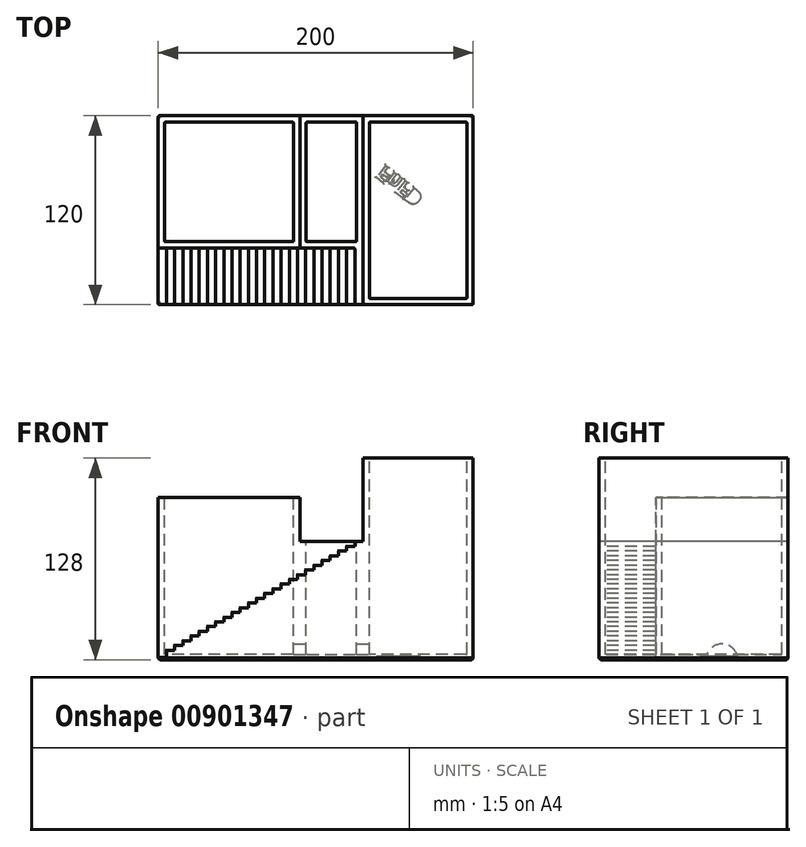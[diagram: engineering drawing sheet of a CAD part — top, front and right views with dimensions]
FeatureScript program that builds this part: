
annotation { "Feature Type Name" : "Feature", "Feature Type Description" : "" }
export const myFeature = defineFeature(function(context is Context, id is Id, definition is map)
    precondition{}
    {
        {
            var Q0;
            Q0=qCreatedBy(makeId("Top.planeOp"),FACE);
            var sketch = newSketch(context, id + "F0", { "sketchPlane" : qUnion([Q0])});
            skLineSegment(sketch, "E0.bottom", {"start": v(-100, -60) * mm, "end": v(100, -60) * mm});
            skLineSegment(sketch, "E0.top", {"start": v(-100, 60) * mm, "end": v(100, 60) * mm});
            skLineSegment(sketch, "E0.left", {"start": v(-100, -60) * mm, "end": v(-100, 60) * mm});
            skLineSegment(sketch, "E0.right", {"start": v(100, -60) * mm, "end": v(100, 60) * mm});
            skPoint(sketch, "E0.middle", {"position": v(0, 0) * mm});
            skSolve(sketch);
        }
        {
            var Q0;
            Q0=makeQuery(id+"F0.imprint","IMPRINT",FACE,{"disambiguationData":[TD([[makeQuery(id+"F0.imprint","IMPRINT",EDGE,{"derivedFrom":sQuery(id+"F0.wireOp",EDGE,"E0.bottom")}),1.0]])]});
            extrude(context, id + "F1", {"entities" : qUnion([Q0]), "depth" : 128 * mm, "offsetDistance" : 25 * mm});
        }
        {
            var Q0;
            Q0=makeQuery(id+"F1.opExtrude","SWEPT_FACE",FACE,{"disambiguationData":[OSD([sQuery(id+"F0.wireOp",EDGE,"E0.bottom")])]});
            var sketch = newSketch(context, id + "F2", { "sketchPlane" : qUnion([Q0])});
            skLineSegment(sketch, "E1.bottom", {"start": v(-100, 128) * mm, "end": v(30, 128) * mm});
            skLineSegment(sketch, "E1.top", {"start": v(-100, 75) * mm, "end": v(30, 75) * mm});
            skLineSegment(sketch, "E1.left", {"start": v(-100, 128) * mm, "end": v(-100, 75) * mm});
            skLineSegment(sketch, "E1.right", {"start": v(30, 128) * mm, "end": v(30, 75) * mm});
            skLineSegment(sketch, "E2", {"start": v(-100, 0) * mm, "end": v(30, 75) * mm, "construction": true});
            skLineSegment(sketch, "E3", {"start": v(-100, 0) * mm, "end": v(-100, 3) * mm});
            skLineSegment(sketch, "E4", {"start": v(-100, 3) * mm, "end": v(-94.8, 3) * mm});
            skLineSegment(sketch, "E5", {"start": v(-94.8, 3) * mm, "end": v(-94.8, 6) * mm});
            skLineSegment(sketch, "E6", {"start": v(-94.8, 6) * mm, "end": v(-89.6, 6) * mm});
            skLineSegment(sketch, "E7", {"start": v(-89.6, 6) * mm, "end": v(-89.6, 9) * mm});
            skLineSegment(sketch, "E8", {"start": v(-89.6, 9) * mm, "end": v(-84.4, 9) * mm});
            skLineSegment(sketch, "E9", {"start": v(-84.4, 9) * mm, "end": v(-84.4, 12) * mm});
            skLineSegment(sketch, "E10", {"start": v(-84.4, 12) * mm, "end": v(-79.2, 12) * mm});
            skLineSegment(sketch, "E11", {"start": v(-79.2, 12) * mm, "end": v(-79.2, 15) * mm});
            skLineSegment(sketch, "E12", {"start": v(-79.2, 15) * mm, "end": v(-74, 15) * mm});
            skLineSegment(sketch, "E13", {"start": v(-74, 15) * mm, "end": v(-74, 18) * mm});
            skLineSegment(sketch, "E14", {"start": v(-74, 18) * mm, "end": v(-68.8, 18) * mm});
            skLineSegment(sketch, "E15", {"start": v(-68.8, 18) * mm, "end": v(-68.8, 21) * mm});
            skLineSegment(sketch, "E16", {"start": v(-68.8, 21) * mm, "end": v(-63.6, 21) * mm});
            skLineSegment(sketch, "E17", {"start": v(-63.6, 21) * mm, "end": v(-63.6, 24) * mm});
            skLineSegment(sketch, "E18", {"start": v(-63.6, 24) * mm, "end": v(-58.4, 24) * mm});
            skLineSegment(sketch, "E19", {"start": v(-58.4, 24) * mm, "end": v(-58.4, 27) * mm});
            skLineSegment(sketch, "E20", {"start": v(-58.4, 27) * mm, "end": v(-53.2, 27) * mm});
            skLineSegment(sketch, "E21", {"start": v(-53.2, 27) * mm, "end": v(-53.2, 30) * mm});
            skLineSegment(sketch, "E22", {"start": v(-53.2, 30) * mm, "end": v(-48, 30) * mm});
            skLineSegment(sketch, "E23", {"start": v(-48, 30) * mm, "end": v(-48, 33) * mm});
            skLineSegment(sketch, "E24", {"start": v(-48, 33) * mm, "end": v(-42.8, 33) * mm});
            skLineSegment(sketch, "E25", {"start": v(-42.8, 33) * mm, "end": v(-42.8, 36) * mm});
            skLineSegment(sketch, "E26", {"start": v(-42.8, 36) * mm, "end": v(-37.6, 36) * mm});
            skLineSegment(sketch, "E27", {"start": v(-37.6, 36) * mm, "end": v(-37.6, 39) * mm});
            skLineSegment(sketch, "E28", {"start": v(-37.6, 39) * mm, "end": v(-32.4, 39) * mm});
            skLineSegment(sketch, "E29", {"start": v(-32.4, 39) * mm, "end": v(-32.4, 42) * mm});
            skLineSegment(sketch, "E30", {"start": v(-32.4, 42) * mm, "end": v(-27.2, 42) * mm});
            skLineSegment(sketch, "E31", {"start": v(-27.2, 42) * mm, "end": v(-27.2, 45) * mm});
            skLineSegment(sketch, "E32", {"start": v(-27.2, 45) * mm, "end": v(-22, 45) * mm});
            skLineSegment(sketch, "E33", {"start": v(-22, 45) * mm, "end": v(-22, 48) * mm});
            skLineSegment(sketch, "E34", {"start": v(-22, 48) * mm, "end": v(-16.8, 48) * mm});
            skLineSegment(sketch, "E35", {"start": v(-16.8, 48) * mm, "end": v(-16.8, 51) * mm});
            skLineSegment(sketch, "E36", {"start": v(-16.8, 51) * mm, "end": v(-11.6, 51) * mm});
            skLineSegment(sketch, "E37", {"start": v(-11.6, 51) * mm, "end": v(-11.6, 54) * mm});
            skLineSegment(sketch, "E38", {"start": v(-11.6, 54) * mm, "end": v(-6.4, 54) * mm});
            skLineSegment(sketch, "E39", {"start": v(-6.4, 54) * mm, "end": v(-6.4, 57) * mm});
            skLineSegment(sketch, "E40", {"start": v(-6.4, 57) * mm, "end": v(-1.2, 57) * mm});
            skLineSegment(sketch, "E41", {"start": v(-1.2, 57) * mm, "end": v(-1.2, 60) * mm});
            skLineSegment(sketch, "E42", {"start": v(-1.2, 60) * mm, "end": v(4, 60) * mm});
            skLineSegment(sketch, "E43", {"start": v(4, 60) * mm, "end": v(4, 63) * mm});
            skLineSegment(sketch, "E44", {"start": v(4, 63) * mm, "end": v(9.2, 63) * mm});
            skLineSegment(sketch, "E45", {"start": v(9.2, 63) * mm, "end": v(9.2, 63) * mm});
            skLineSegment(sketch, "E46", {"start": v(9.2, 63) * mm, "end": v(9.2, 66) * mm});
            skLineSegment(sketch, "E47", {"start": v(9.2, 66) * mm, "end": v(14.4, 66) * mm});
            skLineSegment(sketch, "E48", {"start": v(14.4, 66) * mm, "end": v(14.4, 69) * mm});
            skLineSegment(sketch, "E49", {"start": v(14.4, 69) * mm, "end": v(19.6, 69) * mm});
            skLineSegment(sketch, "E50", {"start": v(19.6, 69) * mm, "end": v(19.6, 72) * mm});
            skLineSegment(sketch, "E51", {"start": v(19.6, 72) * mm, "end": v(24.8, 72) * mm});
            skLineSegment(sketch, "E52", {"start": v(24.8, 72) * mm, "end": v(24.8, 75) * mm});
            skLineSegment(sketch, "E53", {"start": v(24.8, 75) * mm, "end": v(30, 75) * mm});
            skLineSegment(sketch, "E54", {"start": v(30, 75) * mm, "end": v(30, 78) * mm});
            skLineSegment(sketch, "E55.bottom", {"start": v(30, 75) * mm, "end": v(-10.09, 75) * mm});
            skLineSegment(sketch, "E55.top", {"start": v(30, 128) * mm, "end": v(-10.09, 128) * mm});
            skLineSegment(sketch, "E55.left", {"start": v(30, 75) * mm, "end": v(30, 128) * mm});
            skLineSegment(sketch, "E55.right", {"start": v(-10.09, 75) * mm, "end": v(-10.09, 128) * mm});
            skSolve(sketch);
        }
        {
            var Q0;
            {var subQ4=sQuery(id+"F2.wireOp",EDGE,"E55.right");Q0=makeQuery(id+"F2.imprint","IMPRINT",FACE,{"disambiguationData":[TD([[makeQuery(id+"F2.imprint","IMPRINT",EDGE,{"derivedFrom":subQ4}),-1.0]])]});}
            extrude(context, id + "F3", {"entities" : qUnion([Q0]), "operationType" : NewBodyOperationType.REMOVE, "endBound" : BoundingType.UP_TO_NEXT, "oppositeDirection" : true, "depth" : 25 * mm, "offsetDistance" : 25 * mm});
        }
        {
            var Q0;
            {var subQ5=sQuery(id+"F2.wireOp",EDGE,"E4");Q0=makeQuery(id+"F2.imprint","IMPRINT",FACE,{"disambiguationData":[TD([[makeQuery(id+"F2.imprint","IMPRINT",EDGE,{"derivedFrom":subQ5}),1.0]])]});}
            var Q1;
            {var subQ0=sQuery(id+"F2.wireOp",EDGE,"E1.left");Q1=makeQuery(id+"F2.imprint","IMPRINT",FACE,{"disambiguationData":[TD([[makeQuery(id+"F2.imprint","IMPRINT",EDGE,{"derivedFrom":subQ0}),1.0]])]});}
            extrude(context, id + "F4", {"entities" : qUnion([Q0, Q1]), "operationType" : NewBodyOperationType.REMOVE, "oppositeDirection" : true, "depth" : 36 * mm, "offsetDistance" : 25 * mm});
        }
        {
            var Q0;
            {var subQ0=sQuery(id+"F0.wireOp",EDGE,"E0.bottom");var subQ1=sQuery(id+"F0.wireOp",EDGE,"E0.top");var subQ2=sQuery(id+"F0.wireOp",EDGE,"E0.left");Q0=makeQuery(id+"F3.boolean.opBoolean","SPLIT",FACE,{"disambiguationData":[TD([makeQuery(id+"F1.opExtrude","SWEPT_FACE",FACE,{"disambiguationData":[OSD([subQ2])]})])],"derivedFrom":makeQuery(id+"F1.opExtrude","CAP_FACE",FACE,{"disambiguationData":[OSD([subQ0,subQ1,subQ2,sQuery(id+"F0.wireOp",EDGE,"E0.right")])],"isStart":false})});}
            extrude(context, id + "F5", {"entities" : qUnion([Q0]), "operationType" : NewBodyOperationType.REMOVE, "oppositeDirection" : true, "depth" : 25 * mm, "offsetDistance" : 25 * mm});
        }
        {
            var Q0;
            Q0=makeQuery(id+"F5.boolean.opBoolean","COPY",FACE,{"derivedFrom":makeQuery(id+"F5.opExtrude","CAP_FACE",FACE,{"disambiguationData":[OSD([sQuery(id+"F0.wireOp",EDGE,"E0.bottom"),sQuery(id+"F0.wireOp",EDGE,"E0.top"),sQuery(id+"F0.wireOp",EDGE,"E0.left"),sQuery(id+"F0.wireOp",EDGE,"E0.right")])],"isStart":false})});
            var sketch = newSketch(context, id + "F6", { "sketchPlane" : qUnion([Q0])});
            skLineSegment(sketch, "E56.0", {"start": v(-96, -20) * mm, "end": v(-14.09, -20) * mm});
            skLineSegment(sketch, "E56.1", {"start": v(-96, -20) * mm, "end": v(-96, 56) * mm});
            skLineSegment(sketch, "E56.2", {"start": v(-96, 56) * mm, "end": v(-14.09, 56) * mm});
            skLineSegment(sketch, "E56.3", {"start": v(-14.09, 56) * mm, "end": v(-14.09, -20) * mm});
            skSolve(sketch);
        }
        {
            var Q0;
            {var subQ0=sQuery(id+"F0.wireOp",EDGE,"E0.bottom");var subQ1=sQuery(id+"F0.wireOp",EDGE,"E0.right");var subQ2=sQuery(id+"F0.wireOp",EDGE,"E0.top");Q0=makeQuery(id+"F3.boolean.opBoolean","SPLIT",FACE,{"disambiguationData":[TD([makeQuery(id+"F1.opExtrude","SWEPT_FACE",FACE,{"disambiguationData":[OSD([subQ1])]})])],"derivedFrom":makeQuery(id+"F1.opExtrude","CAP_FACE",FACE,{"disambiguationData":[OSD([subQ0,subQ2,sQuery(id+"F0.wireOp",EDGE,"E0.left"),subQ1])],"isStart":false})});}
            var sketch = newSketch(context, id + "F7", { "sketchPlane" : qUnion([Q0])});
            skLineSegment(sketch, "E57.0", {"start": v(34, 56) * mm, "end": v(96, 56) * mm});
            skLineSegment(sketch, "E57.1", {"start": v(34, 56) * mm, "end": v(34, -56) * mm});
            skLineSegment(sketch, "E57.2", {"start": v(34, -56) * mm, "end": v(96, -56) * mm});
            skLineSegment(sketch, "E57.3", {"start": v(96, -56) * mm, "end": v(96, 56) * mm});
            skSolve(sketch);
        }
        {
            var Q0;
            Q0=makeQuery(id+"F3.boolean.opBoolean","COPY",FACE,{"derivedFrom":makeQuery(id+"F3.opExtrude","SWEPT_FACE",FACE,{"disambiguationData":[OSD([sQuery(id+"F2.wireOp",EDGE,"E1.top")])]})});
            var sketch = newSketch(context, id + "F8", { "sketchPlane" : qUnion([Q0])});
            skLineSegment(sketch, "E58.bottom", {"start": v(30, 60) * mm, "end": v(-10.09, 60) * mm, "construction": true});
            skLineSegment(sketch, "E58.top", {"start": v(30, -24) * mm, "end": v(-10.09, -24) * mm, "construction": true});
            skLineSegment(sketch, "E58.left", {"start": v(30, 60) * mm, "end": v(30, -24) * mm, "construction": true});
            skLineSegment(sketch, "E58.right", {"start": v(-10.09, 60) * mm, "end": v(-10.09, -24) * mm, "construction": true});
            skPoint(sketch, "E58.middle", {"position": v(9.96, 18) * mm});
            skPoint(sketch, "E58.middle.positionSnap0", {"position": v(9.96, 60) * mm});
            skPoint(sketch, "E58.middle.positionSnap1", {"position": v(-10.09, 18) * mm});
            skPoint(sketch, "E58.centerSnap0", {"position": v(9.96, 60) * mm});
            skPoint(sketch, "E58.centerSnap1", {"position": v(-10.09, 18) * mm});
            skLineSegment(sketch, "E59.0", {"start": v(26, -20) * mm, "end": v(-6.09, -20) * mm});
            skLineSegment(sketch, "E59.1", {"start": v(26, 56) * mm, "end": v(26, -20) * mm});
            skLineSegment(sketch, "E59.2", {"start": v(26, 56) * mm, "end": v(-6.09, 56) * mm});
            skLineSegment(sketch, "E59.3", {"start": v(-6.09, 56) * mm, "end": v(-6.09, -20) * mm});
            skSolve(sketch);
        }
        {
            var Q0;
            Q0=makeQuery(id+"F8.imprint","IMPRINT",FACE,{"disambiguationData":[TD([[makeQuery(id+"F8.imprint","IMPRINT",EDGE,{"derivedFrom":sQuery(id+"F8.wireOp",EDGE,"E59.0")}),-1.0]])]});
            var Q1;
            Q1=makeQuery(id+"F7.imprint","IMPRINT",FACE,{"disambiguationData":[TD([[makeQuery(id+"F7.imprint","IMPRINT",EDGE,{"derivedFrom":sQuery(id+"F7.wireOp",EDGE,"E57.0")}),-1.0]])]});
            var Q2;
            Q2=makeQuery(id+"F6.imprint","IMPRINT",FACE,{"disambiguationData":[TD([[makeQuery(id+"F6.imprint","IMPRINT",EDGE,{"derivedFrom":sQuery(id+"F6.wireOp",EDGE,"E56.0")}),1.0]])]});
            extrude(context, id + "F9", {"entities" : qUnion([Q0, Q1, Q2]), "operationType" : NewBodyOperationType.REMOVE, "endBound" : BoundingType.UP_TO_NEXT, "oppositeDirection" : true, "depth" : 25 * mm, "offsetDistance" : 25 * mm});
        }
        {
            var Q0;
            Q0=makeQuery(id+"F9.boolean.opBoolean","COPY",FACE,{"derivedFrom":makeQuery(id+"F9.opExtrude","SWEPT_FACE",FACE,{"disambiguationData":[OSD([sQuery(id+"F8.wireOp",EDGE,"E59.3")])]})});
            var sketch = newSketch(context, id + "F10", { "sketchPlane" : qUnion([Q0])});
            skArc(sketch, "E60", {"start": v(28, 0) * mm, "mid": v(18, 10) * mm, "end": v(8, 0) * mm});
            skSolve(sketch);
        }
        {
            var Q0;
            {var subQ0=sQuery(id+"F10.wireOp",EDGE,"E60");Q0=makeQuery(id+"F10.imprint","IMPRINT",FACE,{"disambiguationData":[TD([[makeQuery(id+"F10.imprint","IMPRINT",EDGE,{"derivedFrom":subQ0}),1.0]])]});}
            extrude(context, id + "F11", {"entities" : qUnion([Q0]), "operationType" : NewBodyOperationType.REMOVE, "endBound" : BoundingType.SYMMETRIC, "oppositeDirection" : true, "depth" : 100 * mm, "offsetDistance" : 25 * mm});
        }
        {
            var Q0;
            Q0=makeQuery(id+"F0.imprint","IMPRINT",FACE,{"disambiguationData":[TD([[makeQuery(id+"F0.imprint","IMPRINT",EDGE,{"derivedFrom":sQuery(id+"F0.wireOp",EDGE,"E0.bottom")}),1.0]])]});
            extrude(context, id + "F12", {"entities" : qUnion([Q0]), "operationType" : NewBodyOperationType.ADD, "depth" : 3.5 * mm, "offsetDistance" : 25 * mm});
        }
        {
            var Q0;
            {var subQ0=sQuery(id+"F0.wireOp",EDGE,"E0.right");var subQ1=sQuery(id+"F0.wireOp",EDGE,"E0.left");var subQ2=sQuery(id+"F0.wireOp",EDGE,"E0.top");var subQ3=sQuery(id+"F0.wireOp",EDGE,"E0.bottom");Q0=makeQuery(id+"F12.boolean.opBoolean","MERGE",FACE,{"derivedFrom":[makeQuery(id+"F1.opExtrude","CAP_FACE",FACE,{"disambiguationData":[OSD([subQ3,subQ2,subQ1,subQ0])],"isStart":true}),makeQuery(id+"F12.opExtrude","CAP_FACE",FACE,{"disambiguationData":[OSD([subQ3,subQ2,subQ1,subQ0])],"isStart":true})]});}
            chamfer(context, id + "F13", {"entities" : qUnion([Q0]), "width" : 1 * mm, "tangentPropagation" : true});
        }
        {
            var Q0;
            {var subQ0=sQuery(id+"F0.wireOp",EDGE,"E0.right");var subQ1=sQuery(id+"F0.wireOp",EDGE,"E0.left");var subQ2=sQuery(id+"F0.wireOp",EDGE,"E0.top");var subQ3=sQuery(id+"F0.wireOp",EDGE,"E0.bottom");Q0=makeQuery(id+"F12.boolean.opBoolean","MERGE",FACE,{"derivedFrom":[makeQuery(id+"F1.opExtrude","CAP_FACE",FACE,{"disambiguationData":[OSD([subQ3,subQ2,subQ1,subQ0])],"isStart":true}),makeQuery(id+"F12.opExtrude","CAP_FACE",FACE,{"disambiguationData":[OSD([subQ3,subQ2,subQ1,subQ0])],"isStart":true})]});}
            var sketch = newSketch(context, id + "F14", { "sketchPlane" : qUnion([Q0])});
            skText(sketch, "E61", { "text": "FnFD", "fontName": "OpenSans-Bold.ttf"});
            const initialGuessF14  = {"E61": [0.04341, -0.029, 0.7879, 0.6158, 0.00935]};
            skSetInitialGuess(sketch, initialGuessF14);
            skSolve(sketch);
        }
        {
            var Q0;
            Q0=qSketchRegion(id+"F14",true);
            var Q1;
            Q1=makeQuery(id+"F14.imprint","IMPRINT",FACE,{"disambiguationData":[TD([[makeQuery(id+"F14.imprint","IMPRINT",EDGE,{"derivedFrom":sQuery(id+"F14.wireOp",EDGE,"E61.sketch_text.stroke-44")}),1.0]])]});
            extrude(context, id + "F15", {"entities" : qUnion([Q0, Q1]), "operationType" : NewBodyOperationType.REMOVE, "oppositeDirection" : true, "depth" : 2 * mm, "offsetDistance" : 25 * mm});
        }
        {
            var Q0;
            Q0=makeQuery(id+"F15.boolean.opBoolean","COPY",EDGE,{"derivedFrom":makeQuery(id+"F15.opExtrude","CAP_EDGE",EDGE,{"disambiguationData":[OSD([sQuery(id+"F14.wireOp",EDGE,"E61.sketch_text.stroke-5")])],"isStart":true})});
            var Q1;
            Q1=makeQuery(id+"F15.boolean.opBoolean","COPY",EDGE,{"derivedFrom":makeQuery(id+"F15.opExtrude","CAP_EDGE",EDGE,{"disambiguationData":[OSD([sQuery(id+"F14.wireOp",EDGE,"E61.sketch_text.stroke-4")])],"isStart":true})});
            var Q2;
            Q2=makeQuery(id+"F15.boolean.opBoolean","COPY",EDGE,{"derivedFrom":makeQuery(id+"F15.opExtrude","CAP_EDGE",EDGE,{"disambiguationData":[OSD([sQuery(id+"F14.wireOp",EDGE,"E61.sketch_text.stroke-3")])],"isStart":true})});
            var Q3;
            Q3=makeQuery(id+"F15.boolean.opBoolean","COPY",EDGE,{"derivedFrom":makeQuery(id+"F15.opExtrude","CAP_EDGE",EDGE,{"disambiguationData":[OSD([sQuery(id+"F14.wireOp",EDGE,"E61.sketch_text.stroke-2")])],"isStart":true})});
            var Q4;
            Q4=makeQuery(id+"F15.boolean.opBoolean","COPY",EDGE,{"derivedFrom":makeQuery(id+"F15.opExtrude","CAP_EDGE",EDGE,{"disambiguationData":[OSD([sQuery(id+"F14.wireOp",EDGE,"E61.sketch_text.stroke-1")])],"isStart":true})});
            var Q5;
            Q5=makeQuery(id+"F15.boolean.opBoolean","COPY",EDGE,{"derivedFrom":makeQuery(id+"F15.opExtrude","CAP_EDGE",EDGE,{"disambiguationData":[OSD([sQuery(id+"F14.wireOp",EDGE,"E61.sketch_text.stroke-0")])],"isStart":true})});
            var Q6;
            {var subQ0=sQuery(id+"F0.wireOp",EDGE,"E0.bottom");var subQ1=sQuery(id+"F0.wireOp",EDGE,"E0.top");var subQ2=sQuery(id+"F0.wireOp",EDGE,"E0.left");var subQ3=sQuery(id+"F0.wireOp",EDGE,"E0.right");Q6=makeQuery(id+"F15.boolean.opBoolean","SPLIT",FACE,{"disambiguationData":[TD([makeQuery(id+"F13.opChamfer","BLEND_FACE",FACE,{"disambiguationData":[OSD([subQ0])]})])],"derivedFrom":makeQuery(id+"F12.boolean.opBoolean","MERGE",FACE,{"derivedFrom":[makeQuery(id+"F1.opExtrude","CAP_FACE",FACE,{"disambiguationData":[OSD([subQ0,subQ1,subQ2,subQ3])],"isStart":true}),makeQuery(id+"F12.opExtrude","CAP_FACE",FACE,{"disambiguationData":[OSD([subQ0,subQ1,subQ2,subQ3])],"isStart":true})]})});}
            var Q7;
            Q7=makeQuery(id+"F15.boolean.opBoolean","COPY",EDGE,{"derivedFrom":makeQuery(id+"F15.opExtrude","CAP_EDGE",EDGE,{"disambiguationData":[OSD([sQuery(id+"F14.wireOp",EDGE,"E61.sketch_text.stroke-8")])],"isStart":true})});
            fillet(context, id + "F16", {"entities" : qUnion([Q0, Q1, Q2, Q3, Q4, Q5, Q6, Q7]), "radius" : 1 * mm, "tangentPropagation" : true, "allowEdgeOverflow" : false});
        }
        {
            var Q0;
            Q0=makeQuery(id+"F4.boolean.opBoolean","COPY",EDGE,{"derivedFrom":makeQuery(id+"F4.opExtrude","CAP_EDGE",EDGE,{"disambiguationData":[OSD([sQuery(id+"F2.wireOp",EDGE,"E15")])],"isStart":true})});
            var Q1;
            Q1=makeQuery(id+"F4.boolean.opBoolean","COPY",EDGE,{"derivedFrom":makeQuery(id+"F4.opExtrude","CAP_EDGE",EDGE,{"disambiguationData":[OSD([sQuery(id+"F2.wireOp",EDGE,"E13")])],"isStart":true})});
            var Q2;
            Q2=makeQuery(id+"F4.boolean.opBoolean","COPY",EDGE,{"derivedFrom":makeQuery(id+"F4.opExtrude","CAP_EDGE",EDGE,{"disambiguationData":[OSD([sQuery(id+"F2.wireOp",EDGE,"E11")])],"isStart":true})});
            var Q3;
            Q3=makeQuery(id+"F4.boolean.opBoolean","COPY",EDGE,{"derivedFrom":makeQuery(id+"F4.opExtrude","CAP_EDGE",EDGE,{"disambiguationData":[OSD([sQuery(id+"F2.wireOp",EDGE,"E9")])],"isStart":true})});
            var Q4;
            Q4=makeQuery(id+"F4.boolean.opBoolean","COPY",EDGE,{"derivedFrom":makeQuery(id+"F4.opExtrude","CAP_EDGE",EDGE,{"disambiguationData":[OSD([sQuery(id+"F2.wireOp",EDGE,"E7")])],"isStart":true})});
            var Q5;
            Q5=makeQuery(id+"F4.boolean.opBoolean","COPY",EDGE,{"derivedFrom":makeQuery(id+"F4.opExtrude","CAP_EDGE",EDGE,{"disambiguationData":[OSD([sQuery(id+"F2.wireOp",EDGE,"E5")])],"isStart":true})});
            var Q6;
            Q6=makeQuery(id+"F1.opExtrude","SWEPT_EDGE",EDGE,{"disambiguationData":[OSD([sQuery(id+"F0.wireOp",EDGE,"E0.bottom"),sQuery(id+"F0.wireOp",EDGE,"E0.left")])]});
            var Q7;
            Q7=makeQuery(id+"F4.boolean.opBoolean","COPY",EDGE,{"derivedFrom":makeQuery(id+"F4.opExtrude","CAP_EDGE",EDGE,{"disambiguationData":[OSD([sQuery(id+"F2.wireOp",EDGE,"E17")])],"isStart":true})});
            var Q8;
            Q8=makeQuery(id+"F4.boolean.opBoolean","COPY",EDGE,{"derivedFrom":makeQuery(id+"F4.opExtrude","CAP_EDGE",EDGE,{"disambiguationData":[OSD([sQuery(id+"F2.wireOp",EDGE,"E21")])],"isStart":true})});
            var Q9;
            Q9=makeQuery(id+"F4.boolean.opBoolean","COPY",EDGE,{"derivedFrom":makeQuery(id+"F4.opExtrude","CAP_EDGE",EDGE,{"disambiguationData":[OSD([sQuery(id+"F2.wireOp",EDGE,"E19")])],"isStart":true})});
            var Q10;
            Q10=makeQuery(id+"F4.boolean.opBoolean","COPY",EDGE,{"derivedFrom":makeQuery(id+"F4.opExtrude","CAP_EDGE",EDGE,{"disambiguationData":[OSD([sQuery(id+"F2.wireOp",EDGE,"E31")])],"isStart":true})});
            var Q11;
            Q11=makeQuery(id+"F4.boolean.opBoolean","COPY",EDGE,{"derivedFrom":makeQuery(id+"F4.opExtrude","CAP_EDGE",EDGE,{"disambiguationData":[OSD([sQuery(id+"F2.wireOp",EDGE,"E29")])],"isStart":true})});
            var Q12;
            Q12=makeQuery(id+"F4.boolean.opBoolean","COPY",EDGE,{"derivedFrom":makeQuery(id+"F4.opExtrude","CAP_EDGE",EDGE,{"disambiguationData":[OSD([sQuery(id+"F2.wireOp",EDGE,"E27")])],"isStart":true})});
            var Q13;
            Q13=makeQuery(id+"F4.boolean.opBoolean","COPY",EDGE,{"derivedFrom":makeQuery(id+"F4.opExtrude","CAP_EDGE",EDGE,{"disambiguationData":[OSD([sQuery(id+"F2.wireOp",EDGE,"E25")])],"isStart":true})});
            var Q14;
            Q14=makeQuery(id+"F4.boolean.opBoolean","COPY",EDGE,{"derivedFrom":makeQuery(id+"F4.opExtrude","CAP_EDGE",EDGE,{"disambiguationData":[OSD([sQuery(id+"F2.wireOp",EDGE,"E23")])],"isStart":true})});
            var Q15;
            Q15=makeQuery(id+"F4.boolean.opBoolean","COPY",EDGE,{"derivedFrom":makeQuery(id+"F4.opExtrude","CAP_EDGE",EDGE,{"disambiguationData":[OSD([sQuery(id+"F2.wireOp",EDGE,"E33")])],"isStart":true})});
            var Q16;
            Q16=makeQuery(id+"F4.boolean.opBoolean","COPY",EDGE,{"derivedFrom":makeQuery(id+"F4.opExtrude","CAP_EDGE",EDGE,{"disambiguationData":[OSD([sQuery(id+"F2.wireOp",EDGE,"E37")])],"isStart":true})});
            var Q17;
            Q17=makeQuery(id+"F4.boolean.opBoolean","COPY",EDGE,{"derivedFrom":makeQuery(id+"F4.opExtrude","CAP_EDGE",EDGE,{"disambiguationData":[OSD([sQuery(id+"F2.wireOp",EDGE,"E35")])],"isStart":true})});
            var Q18;
            Q18=makeQuery(id+"F4.boolean.opBoolean","COPY",EDGE,{"derivedFrom":makeQuery(id+"F4.opExtrude","CAP_EDGE",EDGE,{"disambiguationData":[OSD([sQuery(id+"F2.wireOp",EDGE,"E52")])],"isStart":true})});
            var Q19;
            Q19=makeQuery(id+"F4.boolean.opBoolean","COPY",EDGE,{"derivedFrom":makeQuery(id+"F4.opExtrude","CAP_EDGE",EDGE,{"disambiguationData":[OSD([sQuery(id+"F2.wireOp",EDGE,"E50")])],"isStart":true})});
            var Q20;
            Q20=makeQuery(id+"F4.boolean.opBoolean","COPY",EDGE,{"derivedFrom":makeQuery(id+"F4.opExtrude","CAP_EDGE",EDGE,{"disambiguationData":[OSD([sQuery(id+"F2.wireOp",EDGE,"E48")])],"isStart":true})});
            var Q21;
            Q21=makeQuery(id+"F4.boolean.opBoolean","COPY",EDGE,{"derivedFrom":makeQuery(id+"F4.opExtrude","CAP_EDGE",EDGE,{"disambiguationData":[OSD([sQuery(id+"F2.wireOp",EDGE,"E46")])],"isStart":true})});
            var Q22;
            Q22=makeQuery(id+"F4.boolean.opBoolean","COPY",EDGE,{"derivedFrom":makeQuery(id+"F4.opExtrude","CAP_EDGE",EDGE,{"disambiguationData":[OSD([sQuery(id+"F2.wireOp",EDGE,"E43")])],"isStart":true})});
            var Q23;
            Q23=makeQuery(id+"F4.boolean.opBoolean","COPY",EDGE,{"derivedFrom":makeQuery(id+"F4.opExtrude","CAP_EDGE",EDGE,{"disambiguationData":[OSD([sQuery(id+"F2.wireOp",EDGE,"E41")])],"isStart":true})});
            var Q24;
            Q24=makeQuery(id+"F4.boolean.opBoolean","COPY",EDGE,{"derivedFrom":makeQuery(id+"F4.opExtrude","CAP_EDGE",EDGE,{"disambiguationData":[OSD([sQuery(id+"F2.wireOp",EDGE,"E39")])],"isStart":true})});
            var Q25;
            Q25=makeQuery(id+"F3.boolean.opBoolean","COPY",EDGE,{"derivedFrom":makeQuery(id+"F3.opExtrude","CAP_EDGE",EDGE,{"disambiguationData":[OSD([sQuery(id+"F2.wireOp",EDGE,"E1.right")])],"isStart":true})});
            var Q26;
            Q26=makeQuery(id+"F4.boolean.opBoolean","COPY",EDGE,{"derivedFrom":makeQuery(id+"F4.opExtrude","CAP_EDGE",EDGE,{"disambiguationData":[OSD([sQuery(id+"F2.wireOp",EDGE,"E55.right")])],"isStart":false})});
            var Q27;
            Q27=makeQuery(id+"F4.boolean.opBoolean","COPY",EDGE,{"derivedFrom":makeQuery(id+"F4.opExtrude","CAP_EDGE",EDGE,{"disambiguationData":[OSD([sQuery(id+"F0.wireOp",EDGE,"E0.bottom"),sQuery(id+"F0.wireOp",EDGE,"E0.left"),sQuery(id+"F2.wireOp",EDGE,"E1.left")])],"isStart":false})});
            var Q28;
            Q28=makeQuery(id+"F9.boolean.opBoolean","COPY",EDGE,{"derivedFrom":makeQuery(id+"F9.opExtrude","SWEPT_EDGE",EDGE,{"disambiguationData":[OSD([sQuery(id+"F6.wireOp",EDGE,"E56.2"),sQuery(id+"F6.wireOp",EDGE,"E56.3")])]})});
            var Q29;
            Q29=makeQuery(id+"F3.boolean.opBoolean","COPY",EDGE,{"derivedFrom":makeQuery(id+"F3.opExtrude","CAP_EDGE",EDGE,{"disambiguationData":[OSD([sQuery(id+"F2.wireOp",EDGE,"E1.right")])],"isStart":false})});
            var Q30;
            Q30=makeQuery(id+"F1.opExtrude","SWEPT_EDGE",EDGE,{"disambiguationData":[OSD([sQuery(id+"F0.wireOp",EDGE,"E0.bottom"),sQuery(id+"F0.wireOp",EDGE,"E0.right")])]});
            var Q31;
            Q31=makeQuery(id+"F9.boolean.opBoolean","COPY",EDGE,{"derivedFrom":makeQuery(id+"F9.opExtrude","SWEPT_EDGE",EDGE,{"disambiguationData":[OSD([sQuery(id+"F7.wireOp",EDGE,"E57.2"),sQuery(id+"F7.wireOp",EDGE,"E57.3")])]})});
            var Q32;
            Q32=makeQuery(id+"F1.opExtrude","SWEPT_EDGE",EDGE,{"disambiguationData":[OSD([sQuery(id+"F0.wireOp",EDGE,"E0.top"),sQuery(id+"F0.wireOp",EDGE,"E0.left")])]});
            var Q33;
            Q33=makeQuery(id+"F9.boolean.opBoolean","COPY",EDGE,{"derivedFrom":makeQuery(id+"F9.opExtrude","SWEPT_EDGE",EDGE,{"disambiguationData":[OSD([sQuery(id+"F7.wireOp",EDGE,"E57.1"),sQuery(id+"F7.wireOp",EDGE,"E57.2")])]})});
            var Q34;
            Q34=makeQuery(id+"F9.boolean.opBoolean","COPY",EDGE,{"derivedFrom":makeQuery(id+"F9.opExtrude","SWEPT_EDGE",EDGE,{"disambiguationData":[OSD([sQuery(id+"F6.wireOp",EDGE,"E56.1"),sQuery(id+"F6.wireOp",EDGE,"E56.2")])]})});
            var Q35;
            Q35=makeQuery(id+"F9.boolean.opBoolean","COPY",EDGE,{"derivedFrom":makeQuery(id+"F9.opExtrude","SWEPT_EDGE",EDGE,{"disambiguationData":[OSD([sQuery(id+"F7.wireOp",EDGE,"E57.0"),sQuery(id+"F7.wireOp",EDGE,"E57.1")])]})});
            var Q36;
            Q36=makeQuery(id+"F9.boolean.opBoolean","COPY",EDGE,{"derivedFrom":makeQuery(id+"F9.opExtrude","SWEPT_EDGE",EDGE,{"disambiguationData":[OSD([sQuery(id+"F7.wireOp",EDGE,"E57.0"),sQuery(id+"F7.wireOp",EDGE,"E57.3")])]})});
            var Q37;
            Q37=makeQuery(id+"F9.boolean.opBoolean","COPY",EDGE,{"derivedFrom":makeQuery(id+"F9.opExtrude","SWEPT_EDGE",EDGE,{"disambiguationData":[OSD([sQuery(id+"F6.wireOp",EDGE,"E56.0"),sQuery(id+"F6.wireOp",EDGE,"E56.3")])]})});
            var Q38;
            Q38=makeQuery(id+"F1.opExtrude","SWEPT_EDGE",EDGE,{"disambiguationData":[OSD([sQuery(id+"F0.wireOp",EDGE,"E0.top"),sQuery(id+"F0.wireOp",EDGE,"E0.right")])]});
            var Q39;
            Q39=makeQuery(id+"F9.boolean.opBoolean","COPY",EDGE,{"derivedFrom":makeQuery(id+"F9.opExtrude","SWEPT_EDGE",EDGE,{"disambiguationData":[OSD([sQuery(id+"F6.wireOp",EDGE,"E56.0"),sQuery(id+"F6.wireOp",EDGE,"E56.1")])]})});
            var Q40;
            Q40=makeQuery(id+"F9.boolean.opBoolean","COPY",EDGE,{"derivedFrom":makeQuery(id+"F9.opExtrude","SWEPT_EDGE",EDGE,{"disambiguationData":[OSD([sQuery(id+"F8.wireOp",EDGE,"E59.0"),sQuery(id+"F8.wireOp",EDGE,"E59.3")])]})});
            var Q41;
            Q41=makeQuery(id+"F9.boolean.opBoolean","COPY",EDGE,{"derivedFrom":makeQuery(id+"F9.opExtrude","SWEPT_EDGE",EDGE,{"disambiguationData":[OSD([sQuery(id+"F8.wireOp",EDGE,"E59.0"),sQuery(id+"F8.wireOp",EDGE,"E59.1")])]})});
            var Q42;
            Q42=makeQuery(id+"F9.boolean.opBoolean","COPY",EDGE,{"derivedFrom":makeQuery(id+"F9.opExtrude","SWEPT_EDGE",EDGE,{"disambiguationData":[OSD([sQuery(id+"F8.wireOp",EDGE,"E59.2"),sQuery(id+"F8.wireOp",EDGE,"E59.3")])]})});
            var Q43;
            Q43=makeQuery(id+"F9.boolean.opBoolean","COPY",EDGE,{"derivedFrom":makeQuery(id+"F9.opExtrude","SWEPT_EDGE",EDGE,{"disambiguationData":[OSD([sQuery(id+"F8.wireOp",EDGE,"E59.1"),sQuery(id+"F8.wireOp",EDGE,"E59.2")])]})});
            var Q44;
            Q44=makeQuery(id+"F4.boolean.opBoolean","COPY",EDGE,{"derivedFrom":makeQuery(id+"F4.opExtrude","CAP_EDGE",EDGE,{"disambiguationData":[OSD([sQuery(id+"F2.wireOp",EDGE,"E52")])],"isStart":false})});
            var Q45;
            Q45=makeQuery(id+"F4.boolean.opBoolean","COPY",EDGE,{"derivedFrom":makeQuery(id+"F4.opExtrude","CAP_EDGE",EDGE,{"disambiguationData":[OSD([sQuery(id+"F2.wireOp",EDGE,"E50")])],"isStart":false})});
            var Q46;
            Q46=makeQuery(id+"F4.boolean.opBoolean","COPY",EDGE,{"derivedFrom":makeQuery(id+"F4.opExtrude","CAP_EDGE",EDGE,{"disambiguationData":[OSD([sQuery(id+"F2.wireOp",EDGE,"E48")])],"isStart":false})});
            var Q47;
            Q47=makeQuery(id+"F4.boolean.opBoolean","COPY",EDGE,{"derivedFrom":makeQuery(id+"F4.opExtrude","CAP_EDGE",EDGE,{"disambiguationData":[OSD([sQuery(id+"F2.wireOp",EDGE,"E43")])],"isStart":false})});
            var Q48;
            Q48=makeQuery(id+"F4.boolean.opBoolean","COPY",EDGE,{"derivedFrom":makeQuery(id+"F4.opExtrude","CAP_EDGE",EDGE,{"disambiguationData":[OSD([sQuery(id+"F2.wireOp",EDGE,"E5")])],"isStart":false})});
            var Q49;
            Q49=makeQuery(id+"F4.boolean.opBoolean","COPY",EDGE,{"derivedFrom":makeQuery(id+"F4.opExtrude","CAP_EDGE",EDGE,{"disambiguationData":[OSD([sQuery(id+"F2.wireOp",EDGE,"E7")])],"isStart":false})});
            var Q50;
            Q50=makeQuery(id+"F4.boolean.opBoolean","COPY",EDGE,{"derivedFrom":makeQuery(id+"F4.opExtrude","CAP_EDGE",EDGE,{"disambiguationData":[OSD([sQuery(id+"F2.wireOp",EDGE,"E9")])],"isStart":false})});
            var Q51;
            Q51=makeQuery(id+"F4.boolean.opBoolean","COPY",EDGE,{"derivedFrom":makeQuery(id+"F4.opExtrude","CAP_EDGE",EDGE,{"disambiguationData":[OSD([sQuery(id+"F2.wireOp",EDGE,"E11")])],"isStart":false})});
            var Q52;
            Q52=makeQuery(id+"F4.boolean.opBoolean","COPY",EDGE,{"derivedFrom":makeQuery(id+"F4.opExtrude","CAP_EDGE",EDGE,{"disambiguationData":[OSD([sQuery(id+"F2.wireOp",EDGE,"E13")])],"isStart":false})});
            var Q53;
            Q53=makeQuery(id+"F4.boolean.opBoolean","COPY",EDGE,{"derivedFrom":makeQuery(id+"F4.opExtrude","CAP_EDGE",EDGE,{"disambiguationData":[OSD([sQuery(id+"F2.wireOp",EDGE,"E15")])],"isStart":false})});
            var Q54;
            Q54=makeQuery(id+"F4.boolean.opBoolean","COPY",EDGE,{"derivedFrom":makeQuery(id+"F4.opExtrude","CAP_EDGE",EDGE,{"disambiguationData":[OSD([sQuery(id+"F2.wireOp",EDGE,"E17")])],"isStart":false})});
            var Q55;
            Q55=makeQuery(id+"F4.boolean.opBoolean","COPY",EDGE,{"derivedFrom":makeQuery(id+"F4.opExtrude","CAP_EDGE",EDGE,{"disambiguationData":[OSD([sQuery(id+"F2.wireOp",EDGE,"E19")])],"isStart":false})});
            var Q56;
            Q56=makeQuery(id+"F4.boolean.opBoolean","COPY",EDGE,{"derivedFrom":makeQuery(id+"F4.opExtrude","CAP_EDGE",EDGE,{"disambiguationData":[OSD([sQuery(id+"F2.wireOp",EDGE,"E21")])],"isStart":false})});
            var Q57;
            Q57=makeQuery(id+"F4.boolean.opBoolean","COPY",EDGE,{"derivedFrom":makeQuery(id+"F4.opExtrude","CAP_EDGE",EDGE,{"disambiguationData":[OSD([sQuery(id+"F2.wireOp",EDGE,"E23")])],"isStart":false})});
            var Q58;
            Q58=makeQuery(id+"F4.boolean.opBoolean","COPY",EDGE,{"derivedFrom":makeQuery(id+"F4.opExtrude","CAP_EDGE",EDGE,{"disambiguationData":[OSD([sQuery(id+"F2.wireOp",EDGE,"E25")])],"isStart":false})});
            var Q59;
            Q59=makeQuery(id+"F4.boolean.opBoolean","COPY",EDGE,{"derivedFrom":makeQuery(id+"F4.opExtrude","CAP_EDGE",EDGE,{"disambiguationData":[OSD([sQuery(id+"F2.wireOp",EDGE,"E27")])],"isStart":false})});
            var Q60;
            Q60=makeQuery(id+"F4.boolean.opBoolean","COPY",EDGE,{"derivedFrom":makeQuery(id+"F4.opExtrude","CAP_EDGE",EDGE,{"disambiguationData":[OSD([sQuery(id+"F2.wireOp",EDGE,"E29")])],"isStart":false})});
            var Q61;
            Q61=makeQuery(id+"F4.boolean.opBoolean","COPY",EDGE,{"derivedFrom":makeQuery(id+"F4.opExtrude","CAP_EDGE",EDGE,{"disambiguationData":[OSD([sQuery(id+"F2.wireOp",EDGE,"E31")])],"isStart":false})});
            var Q62;
            Q62=makeQuery(id+"F4.boolean.opBoolean","COPY",EDGE,{"derivedFrom":makeQuery(id+"F4.opExtrude","CAP_EDGE",EDGE,{"disambiguationData":[OSD([sQuery(id+"F2.wireOp",EDGE,"E33")])],"isStart":false})});
            var Q63;
            Q63=makeQuery(id+"F4.boolean.opBoolean","COPY",EDGE,{"derivedFrom":makeQuery(id+"F4.opExtrude","CAP_EDGE",EDGE,{"disambiguationData":[OSD([sQuery(id+"F2.wireOp",EDGE,"E35")])],"isStart":false})});
            var Q64;
            Q64=makeQuery(id+"F4.boolean.opBoolean","COPY",EDGE,{"derivedFrom":makeQuery(id+"F4.opExtrude","CAP_EDGE",EDGE,{"disambiguationData":[OSD([sQuery(id+"F2.wireOp",EDGE,"E37")])],"isStart":false})});
            var Q65;
            Q65=makeQuery(id+"F4.boolean.opBoolean","COPY",EDGE,{"derivedFrom":makeQuery(id+"F4.opExtrude","CAP_EDGE",EDGE,{"disambiguationData":[OSD([sQuery(id+"F2.wireOp",EDGE,"E39")])],"isStart":false})});
            var Q66;
            Q66=makeQuery(id+"F4.boolean.opBoolean","COPY",EDGE,{"derivedFrom":makeQuery(id+"F4.opExtrude","CAP_EDGE",EDGE,{"disambiguationData":[OSD([sQuery(id+"F2.wireOp",EDGE,"E41")])],"isStart":false})});
            var Q67;
            Q67=makeQuery(id+"F4.boolean.opBoolean","COPY",EDGE,{"derivedFrom":makeQuery(id+"F4.opExtrude","CAP_EDGE",EDGE,{"disambiguationData":[OSD([sQuery(id+"F2.wireOp",EDGE,"E46")])],"isStart":false})});
            fillet(context, id + "F17", {"entities" : qUnion([Q0, Q1, Q2, Q3, Q4, Q5, Q6, Q7, Q8, Q9, Q10, Q11, Q12, Q13, Q14, Q15, Q16, Q17, Q18, Q19, Q20, Q21, Q22, Q23, Q24, Q25, Q26, Q27, Q28, Q29, Q30, Q31, Q32, Q33, Q34, Q35, Q36, Q37, Q38, Q39, Q40, Q41, Q42, Q43, Q44, Q45, Q46, Q47, Q48, Q49, Q50, Q51, Q52, Q53, Q54, Q55, Q56, Q57, Q58, Q59, Q60, Q61, Q62, Q63, Q64, Q65, Q66, Q67]), "tangentPropagation" : true, "radius" : 0.6 * mm, "defaultsChanged" : false, "vertexSettings" : [], "allowEdgeOverflow" : false});
        }
        {
            var Q0;
            {var subQ1=sQuery(id+"F0.wireOp",EDGE,"E0.left");var subQ2=sQuery(id+"F0.wireOp",EDGE,"E0.bottom");Q0=makeQuery(id+"F12.boolean.opBoolean","SPLIT",FACE,{"disambiguationData":[TD([makeQuery(id+"F1.opExtrude","SWEPT_FACE",FACE,{"disambiguationData":[OSD([subQ2])]})])],"derivedFrom":makeQuery(id+"F12.opExtrude","CAP_FACE",FACE,{"disambiguationData":[OSD([subQ2,sQuery(id+"F0.wireOp",EDGE,"E0.top"),subQ1,sQuery(id+"F0.wireOp",EDGE,"E0.right")])],"isStart":false})});}
            extrude(context, id + "F18", {"entities" : qUnion([Q0]), "operationType" : NewBodyOperationType.REMOVE, "oppositeDirection" : true, "depth" : 2 * mm, "offsetDistance" : 25 * mm});
        }
    });
